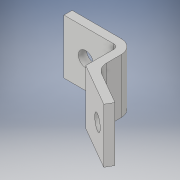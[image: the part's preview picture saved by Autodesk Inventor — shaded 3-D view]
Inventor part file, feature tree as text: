
AUTODESK INVENTOR PART (.ipt)
format: ipt  version: 2019.4 (Build 234330000, 330)  size: 140,800 bytes
history: native  units: mm
features: extrude x3, fillet x2, sketch x2
ambient origin geometry x8: Origin, YZ Plane, XZ Plane, XY Plane, X Axis, Y Axis, Z Axis, Center Point
bodies: Body1 (feature_tree)
feature tree (7):
  extrude  "Extrusion5"  Depth=20.0mm
  extrude  "Extrusion6"  Depth=18.0mm
  extrude  "Extrusion7"  TaperAngle=150.0deg  [1 undecoded]
  fillet  "Fillet1"  Radius=3.0mm
  fillet  "Fillet2"  Radius=3.0mm
  sketch  "Sketch4"  dims[d16=12.0mm d17=20.0mm]
  sketch  "Sketch6"  dims[d18=3.0mm d19=18.0mm d20=150.0deg d21=3.0mm d24=3.0mm d25=20.0mm d26=0.0mm d27=10.0mm d28=5.5mm d29=3.0mm d30=0.0mm d31=10.0mm d32=5.5mm d33=3.0mm d34=0.0mm d35=5.0mm d36=15.0mm d37=2.0mm]
note: 1 required parameter value undecoded (feature->parameter linkage not recoverable at this tier; creation-order binding heuristic only, values carry confidence <= 0.55)
